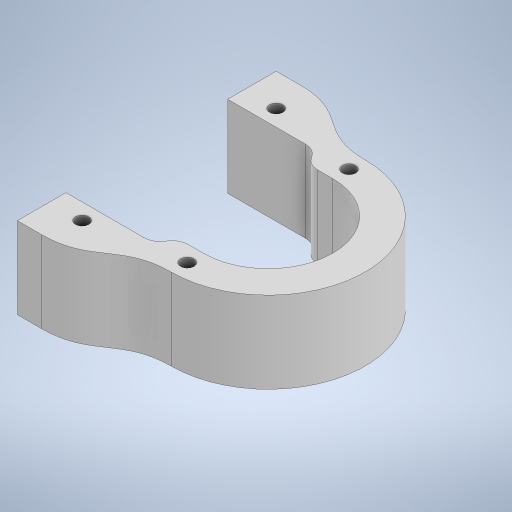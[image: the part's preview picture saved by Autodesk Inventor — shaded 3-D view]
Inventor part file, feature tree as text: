
AUTODESK INVENTOR PART (.ipt)
format: ipt  version: 2024 (Build 280153000, 153)  size: 349,696 bytes
history: native  units: in
note: dims shown in document units (in); Inventor stores cm internally (conversion verified against a paired STEP export)
features: extrude x3, sketch x3
ambient origin geometry x8: Origin, YZ Plane, XZ Plane, XY Plane, X Axis, Y Axis, Z Axis, Center Point
bodies: Solid1 (feature_tree)
feature tree (6):
  extrude  "Extrusion1"  Depth=1.26in TaperAngle=0.0deg
  extrude  "Extrusion2"  Depth=1.06in TaperAngle=0.0deg
  extrude  "Extrusion3"  Depth=0.75in TaperAngle=0.0deg
  sketch  "Sketch1"  dims[d0=1.25in d1=1.26in d2=0.0in]
  sketch  "Sketch2"  dims[d3=0.5in d4=1.06in d5=0.0in]
  sketch  "Sketch3"  dims[d9=0.75in d10=0.5in d11=3.0in d12=4.0in d13=0.25in d14=0.75in d15=0.75in d16=0.75in d17=0.5in d18=3.0in d19=4.0in d20=0.25in d21=0.75in d22=0.75in d23=0.75in d24=0.5in d25=3.0in d26=4.0in d27=0.25in d28=0.75in d29=0.75in d30=0.75in d31=0.5in d32=3.0in d33=4.0in d34=0.25in d35=0.75in d36=0.75in d37=1.06in d38=0.0in]
